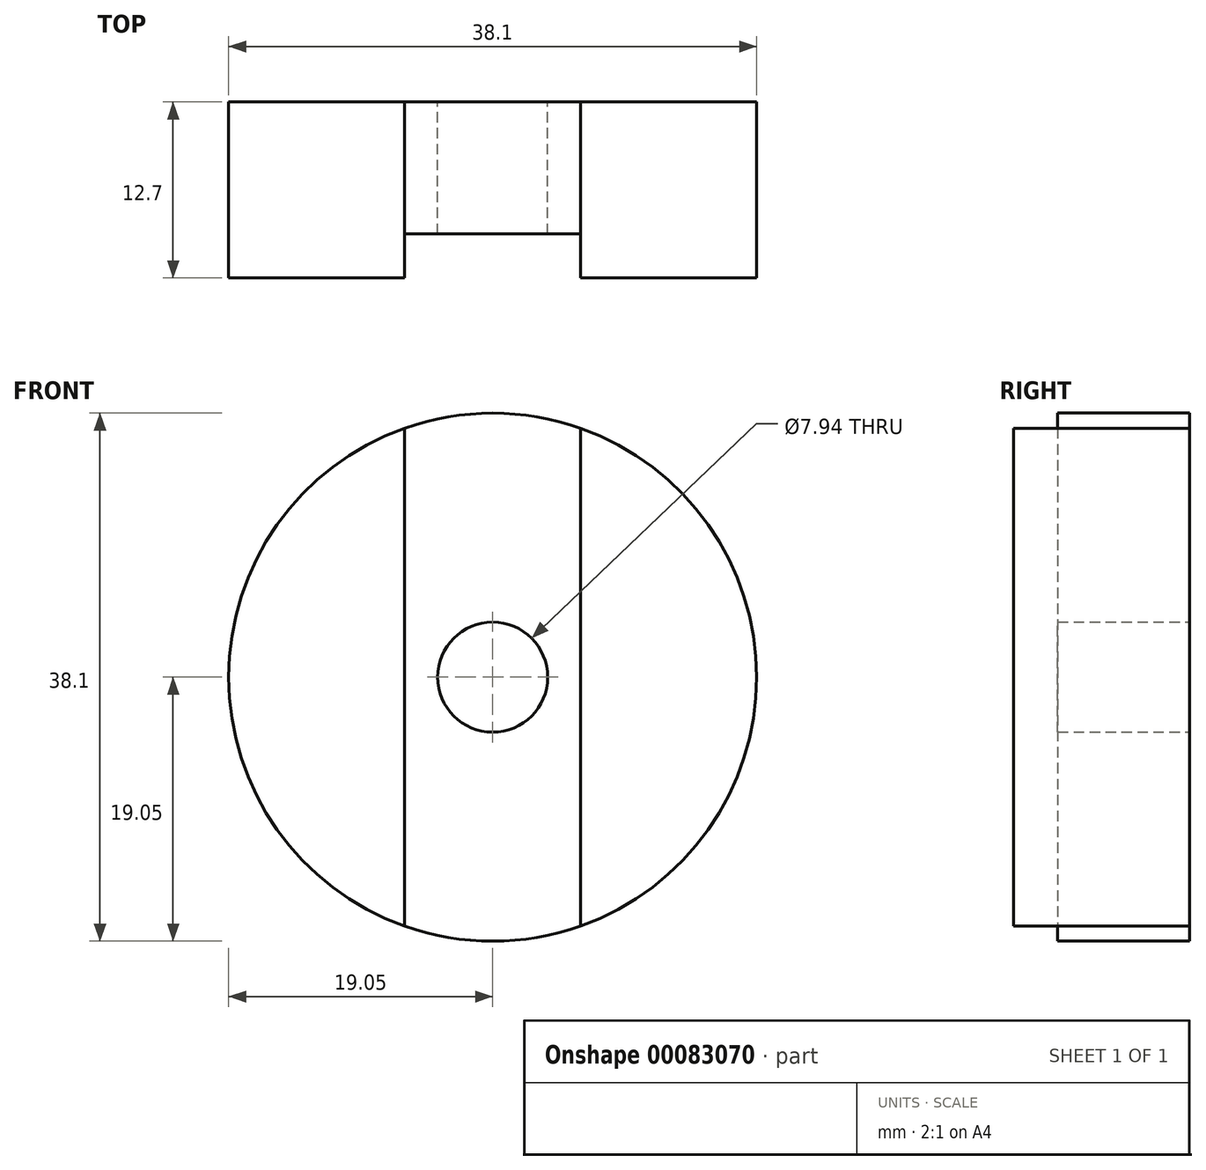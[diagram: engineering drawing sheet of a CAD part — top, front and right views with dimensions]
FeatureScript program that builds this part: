
annotation { "Feature Type Name" : "Feature", "Feature Type Description" : "" }
export const myFeature = defineFeature(function(context is Context, id is Id, definition is map)
    precondition{}
    {
        {
            var Q0;
            Q0=qCreatedBy(makeId("Front.planeOp"),FACE);
            var sketch = newSketch(context, id + "F0", { "sketchPlane" : qUnion([Q0])});
            skCircle(sketch, "E0", {"center": v(0, 0) * mm, "radius": 19.05 * mm});
            skLineSegment(sketch, "E1.bottom", {"start": v(-6.35, 19.05) * mm, "end": v(6.35, 19.05) * mm});
            skLineSegment(sketch, "E1.top", {"start": v(-6.35, -19.05) * mm, "end": v(6.35, -19.05) * mm});
            skLineSegment(sketch, "E1.left", {"start": v(-6.35, 19.05) * mm, "end": v(-6.35, -19.05) * mm});
            skLineSegment(sketch, "E1.right", {"start": v(6.35, 19.05) * mm, "end": v(6.35, -19.05) * mm});
            skCircle(sketch, "E2", {"center": v(0, 0) * mm, "radius": 3.97 * mm});
            skSolve(sketch);
        }
        {
            var Q0;
            {var subQ0=sQuery(id+"F0.wireOp",EDGE,"E1.right");var subQ1=sQuery(id+"F0.wireOp",EDGE,"E0");var subQ2=makeQuery(id+"F0.imprint","INTERSECT",VERTEX,{"disambiguationData":[OD(0.0)],"derivedFrom":[subQ1,subQ0]});Q0=makeQuery(id+"F0.imprint","IMPRINT",FACE,{"disambiguationData":[TD([[makeQuery(id+"F0.imprint","IMPRINT",EDGE,{"disambiguationData":[TD([[subQ2,1.0]])],"derivedFrom":subQ1}),1.0]])]});}
            var Q1;
            {var subQ0=sQuery(id+"F0.wireOp",EDGE,"E1.left");var subQ1=sQuery(id+"F0.wireOp",EDGE,"E0");var subQ2=makeQuery(id+"F0.imprint","INTERSECT",VERTEX,{"disambiguationData":[OD(0.0)],"derivedFrom":[subQ1,subQ0]});Q1=makeQuery(id+"F0.imprint","IMPRINT",FACE,{"disambiguationData":[TD([[makeQuery(id+"F0.imprint","IMPRINT",EDGE,{"disambiguationData":[TD([[subQ2,-1.0]])],"derivedFrom":subQ1}),1.0]])]});}
            extrude(context, id + "F1", {"entities" : qUnion([Q0, Q1]), "depth" : 12.7 * mm});
        }
        {
            var Q0;
            {var subQ0=sQuery(id+"F0.wireOp",EDGE,"E1.left");var subQ1=sQuery(id+"F0.wireOp",EDGE,"E0");var subQ2=makeQuery(id+"F0.imprint","INTERSECT",VERTEX,{"disambiguationData":[OD(0.0)],"derivedFrom":[subQ1,subQ0]});Q0=makeQuery(id+"F0.imprint","IMPRINT",FACE,{"disambiguationData":[TD([[makeQuery(id+"F0.imprint","IMPRINT",EDGE,{"disambiguationData":[TD([[subQ2,1.0]])],"derivedFrom":subQ1}),1.0]])]});}
            extrude(context, id + "F2", {"entities" : qUnion([Q0]), "depth" : 9.52 * mm});
        }
        {
            var Q0;
            Q0=makeQuery(id+"F0.imprint","IMPRINT",FACE,{"disambiguationData":[TD([[makeQuery(id+"F0.imprint","IMPRINT",EDGE,{"derivedFrom":sQuery(id+"F0.wireOp",EDGE,"E2")}),1.0]])]});
            extrude(context, id + "F3", {"entities" : qUnion([Q0]), "operationType" : NewBodyOperationType.REMOVE, "endBound" : BoundingType.THROUGH_ALL, "oppositeDirection" : true, "depth" : 25.4 * mm});
        }
    });
